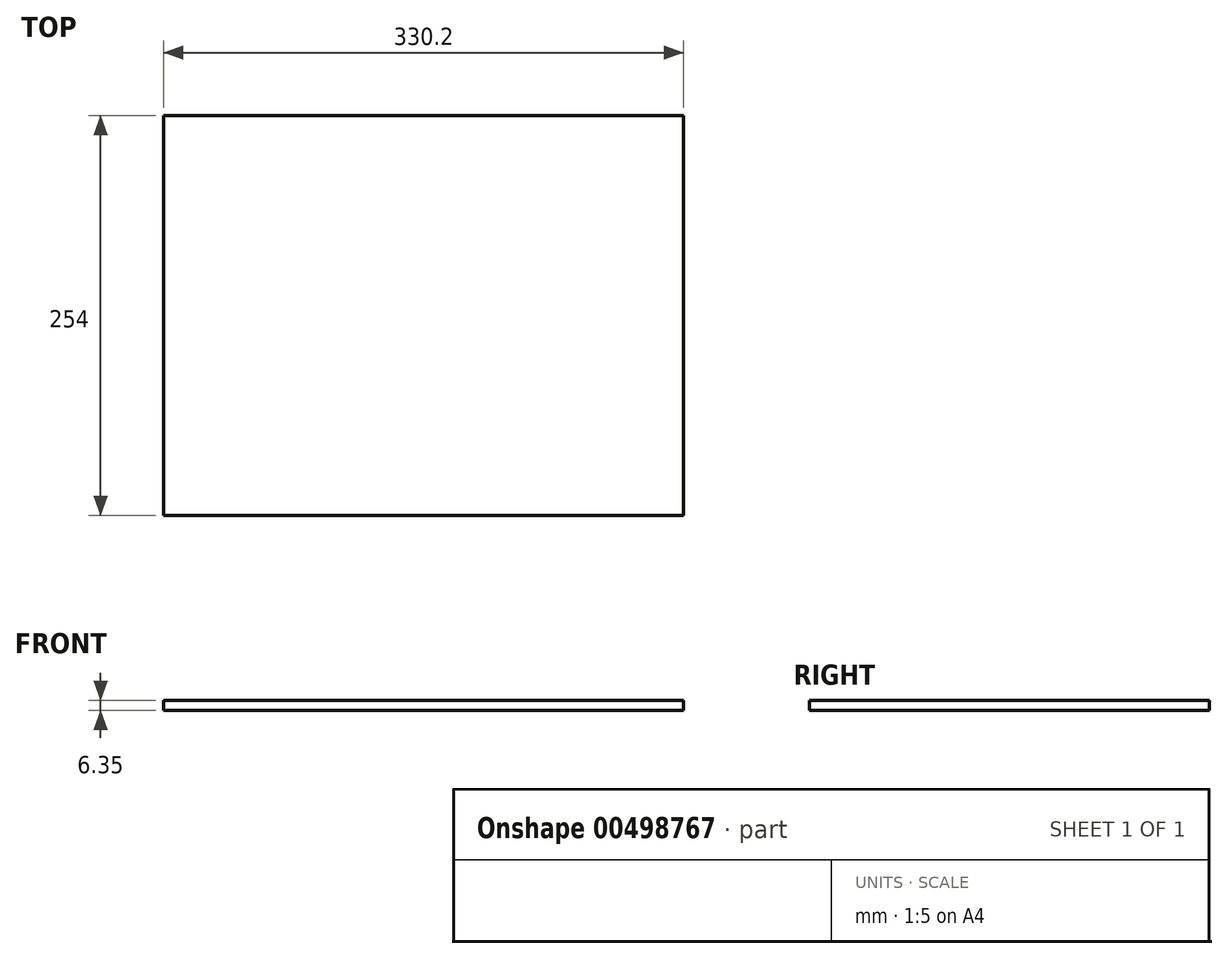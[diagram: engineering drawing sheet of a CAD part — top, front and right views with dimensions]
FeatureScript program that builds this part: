
annotation { "Feature Type Name" : "Feature", "Feature Type Description" : "" }
export const myFeature = defineFeature(function(context is Context, id is Id, definition is map)
    precondition{}
    {
        {
            var Q0;
            Q0=qCreatedBy(makeId("Top.planeOp"),FACE);
            var sketch = newSketch(context, id + "F0", { "sketchPlane" : qUnion([Q0])});
            skLineSegment(sketch, "E0.bottom", {"start": v(0, 0) * mm, "end": v(330.2, 0) * mm});
            skLineSegment(sketch, "E0.top", {"start": v(0, 254) * mm, "end": v(330.2, 254) * mm});
            skLineSegment(sketch, "E0.left", {"start": v(0, 0) * mm, "end": v(0, 254) * mm});
            skLineSegment(sketch, "E0.right", {"start": v(330.2, 0) * mm, "end": v(330.2, 254) * mm});
            skSolve(sketch);
        }
        {
            var Q0;
            Q0=makeQuery(id+"F0.imprint","IMPRINT",FACE,{"disambiguationData":[TD([[makeQuery(id+"F0.imprint","IMPRINT",EDGE,{"derivedFrom":sQuery(id+"F0.wireOp",EDGE,"E0.bottom")}),1.0]])]});
            extrude(context, id + "F1", {"entities" : qUnion([Q0]), "depth" : 6.35 * mm});
        }
    });
